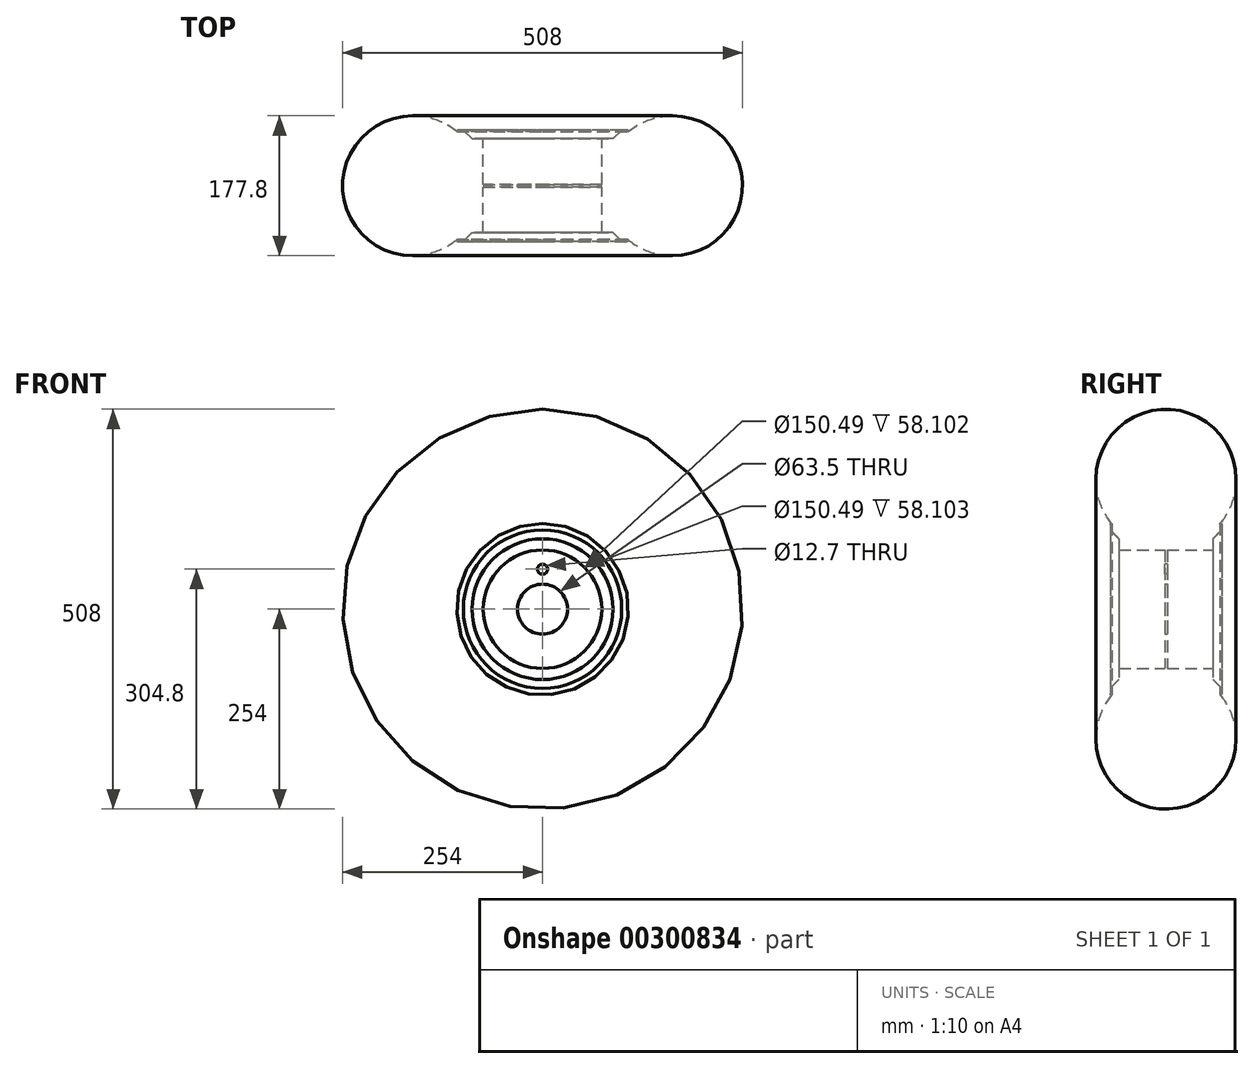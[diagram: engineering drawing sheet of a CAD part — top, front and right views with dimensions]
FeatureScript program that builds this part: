
annotation { "Feature Type Name" : "Feature", "Feature Type Description" : "" }
export const myFeature = defineFeature(function(context is Context, id is Id, definition is map)
    precondition{}
    {
        {
            var Q0;
            Q0=qCreatedBy(makeId("Right.planeOp"),FACE);
            var sketch = newSketch(context, id + "F0", { "sketchPlane" : qUnion([Q0])});
            skArc(sketch, "E0", {"start": v(68.55, 108.5) * mm, "mid": v(0, 254) * mm, "end": v(-68.55, 108.5) * mm});
            skLineSegment(sketch, "E1", {"start": v(0, 0) * mm, "end": v(-203.1, 0) * mm, "construction": true});
            skLineSegment(sketch, "E2", {"start": v(-68.26, 107.7) * mm, "end": v(-68.26, 101.6) * mm});
            skLineSegment(sketch, "E3", {"start": v(-68.26, 101.6) * mm, "end": v(68.26, 101.6) * mm, "construction": true});
            skLineSegment(sketch, "E4", {"start": v(68.26, 101.6) * mm, "end": v(68.26, 107.7) * mm});
            skLineSegment(sketch, "E5", {"start": v(0, 101.6) * mm, "end": v(0, 0) * mm, "construction": true});
            skLineSegment(sketch, "E6", {"start": v(-68.26, 101.6) * mm, "end": v(-57.15, 90.49) * mm});
            skLineSegment(sketch, "E7", {"start": v(-57.15, 90.49) * mm, "end": v(-57.15, 77.79) * mm});
            skLineSegment(sketch, "E8", {"start": v(-57.15, 77.79) * mm, "end": v(57.15, 77.79) * mm});
            skLineSegment(sketch, "E9", {"start": v(57.15, 77.79) * mm, "end": v(57.15, 90.49) * mm});
            skLineSegment(sketch, "E10", {"start": v(57.15, 90.49) * mm, "end": v(68.26, 101.6) * mm});
            skLineSegment(sketch, "E11.0", {"start": v(70.8, 100.55) * mm, "end": v(70.8, 107.7) * mm});
            skLineSegment(sketch, "E11.1", {"start": v(59.69, 89.44) * mm, "end": v(70.8, 100.55) * mm});
            skLineSegment(sketch, "E11.2", {"start": v(59.69, 75.25) * mm, "end": v(59.69, 89.44) * mm});
            skLineSegment(sketch, "E11.3", {"start": v(-70.8, 107.7) * mm, "end": v(-70.8, 100.55) * mm});
            skLineSegment(sketch, "E11.4", {"start": v(-70.8, 100.55) * mm, "end": v(-59.69, 89.44) * mm});
            skLineSegment(sketch, "E11.5", {"start": v(-59.69, 89.44) * mm, "end": v(-59.69, 75.25) * mm});
            skLineSegment(sketch, "E11.6", {"start": v(-59.69, 75.25) * mm, "end": v(59.69, 75.25) * mm});
            skLineSegment(sketch, "E12", {"start": v(-1.59, 75.25) * mm, "end": v(-1.59, 31.75) * mm});
            skLineSegment(sketch, "E13", {"start": v(-1.59, 31.75) * mm, "end": v(1.59, 31.75) * mm});
            skLineSegment(sketch, "E14", {"start": v(1.59, 31.75) * mm, "end": v(1.59, 75.25) * mm});
            skArc(sketch, "E15", {"start": v(70.8, 107.7) * mm, "mid": v(69.53, 108.96) * mm, "end": v(68.26, 107.7) * mm});
            skArc(sketch, "E16", {"start": v(-68.26, 107.7) * mm, "mid": v(-69.53, 108.96) * mm, "end": v(-70.8, 107.7) * mm});
            skSolve(sketch);
        }
        {
            var Q0;
            Q0 = qSketchRegion(id + "F0", true);
            var Q1;
            Q1=sQuery(id+"F0.wireOp",EDGE,"E1");
            revolve(context, id + "F1", {"entities" : qUnion([Q0]), "axis" : qUnion([Q1]), "revolveType" : RevolveType.FULL});
        }
        {
            var Q0;
            Q0=makeQuery(id+"F1.opRevolve","SWEPT_FACE",FACE,{"disambiguationData":[OSD([sQuery(id+"F0.wireOp",EDGE,"E12")])]});
            var sketch = newSketch(context, id + "F2", { "sketchPlane" : qUnion([Q0])});
            skCircle(sketch, "E17", {"center": v(0, 50.8) * mm, "radius": 6.35 * mm});
            skSolve(sketch);
        }
        {
            var Q0;
            Q0 = qSketchRegion(id + "F2", true);
            extrude(context, id + "F3", {"entities" : qUnion([Q0]), "operationType" : NewBodyOperationType.REMOVE, "endBound" : BoundingType.THROUGH_ALL, "oppositeDirection" : true, "depth" : 25.4 * mm});
        }
    });
